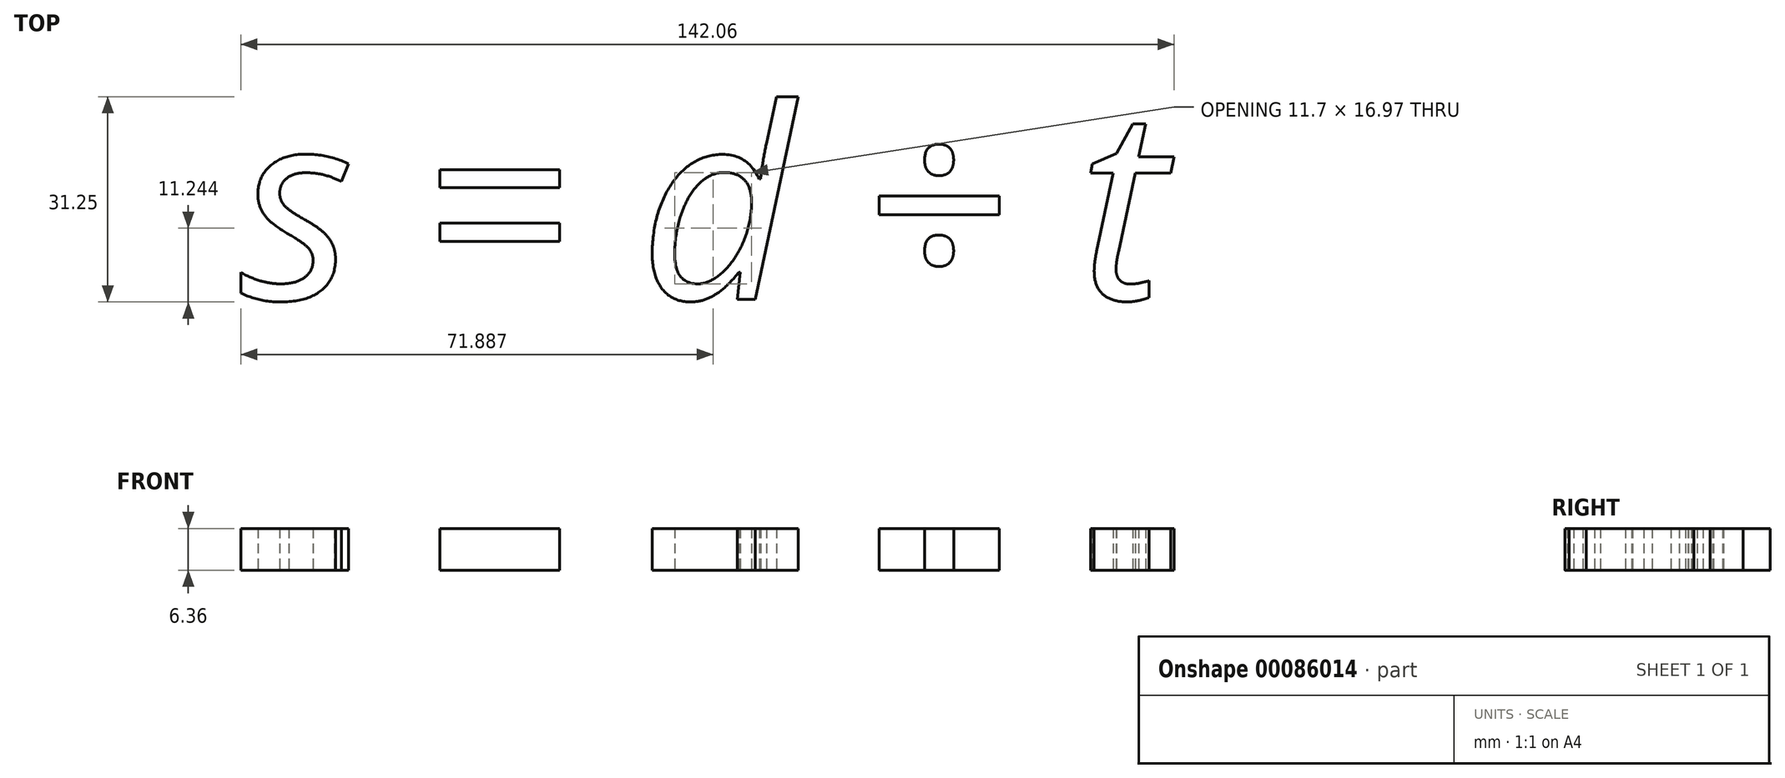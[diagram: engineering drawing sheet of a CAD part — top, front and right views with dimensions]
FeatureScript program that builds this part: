
annotation { "Feature Type Name" : "Feature", "Feature Type Description" : "" }
export const myFeature = defineFeature(function(context is Context, id is Id, definition is map)
    precondition{}
    {
        {
            var Q0;
            Q0=qCreatedBy(makeId("Top.planeOp"),FACE);
            var sketch = newSketch(context, id + "F0", { "sketchPlane" : qUnion([Q0])});
            skText(sketch, "E0", { "text": "s = d ÷ t", "fontName": "OpenSans-Italic.ttf"});
            const initialGuessF0  = {"E0": [-0.06985, -0.01397, 1, 0, 0.02923]};
            skSetInitialGuess(sketch, initialGuessF0);
            skSolve(sketch);
        }
        {
            var Q0;
            Q0 = qSketchRegion(id + "F0", true);
            extrude(context, id + "F1", {"entities" : qUnion([Q0]), "endBound" : BoundingType.SYMMETRIC, "depth" : 6.35 * mm});
        }
    });
